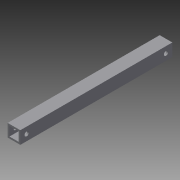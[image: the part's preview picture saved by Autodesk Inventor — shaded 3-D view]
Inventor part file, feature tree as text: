
AUTODESK INVENTOR PART (.ipt)
format: ipt  version: 2013 (Build 170138000, 138)  size: 101,376 bytes
history: native  units: in
note: dims shown in document units (in); Inventor stores cm internally (conversion verified against a paired STEP export)
features: extrude x2, sketch x2
ambient origin geometry x8: Origin, YZ Plane, XZ Plane, XY Plane, X Axis, Y Axis, Z Axis, Center Point
bodies: Solid1 (feature_tree)
feature tree (4):
  extrude  "Extrusion1"  Depth=0.5in
  extrude  "Extrusion2"  Depth=0.43in
  sketch  "Sketch1"  dims[d0=0.5in d1=0.5in]
  sketch  "Sketch2"  dims[d2=0.43in d3=0.43in d4=6.0in d5=0.0in d6=0.168in d7=0.25in d8=0.168in d9=0.25in d10=0.5in d11=0.0in]
